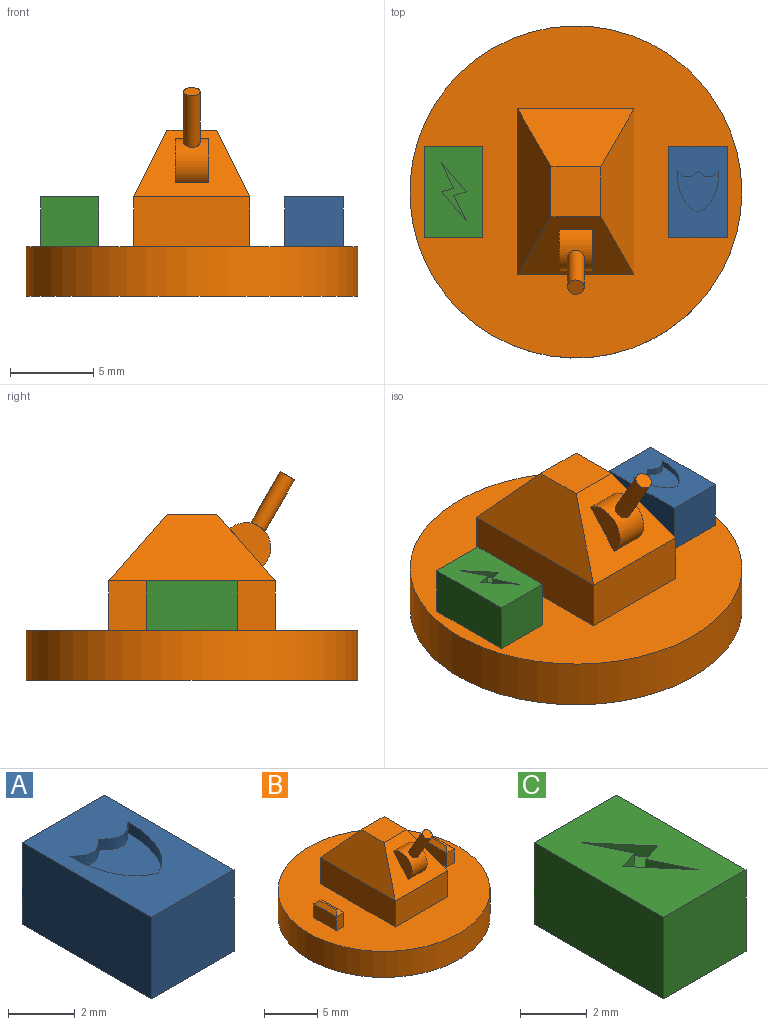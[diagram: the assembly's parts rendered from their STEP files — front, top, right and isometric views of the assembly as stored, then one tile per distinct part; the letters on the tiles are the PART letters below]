
ASSEMBLY  parts=3 mates=2
PART A: 16 faces, bbox 3.5x5.5x3 mm
  f0: plane 5.5x3.5mm, normal (0,0,1), area 15.1mm2, adj f4,f5,f6,f7,f11,f12,f13,f14
  f1: plane 2x1.5mm, normal (0,-1,0), area 3mm2, adj f2,f8,f9,f10
  f2: plane 3.5x2mm, normal (-1,0,0), area 7mm2, adj f1,f3,f9,f10
  f3: plane 2x1.5mm, normal (0,1,0), area 3mm2, adj f2,f8,f9,f10
  f4: plane 5.5x3mm, normal (1,0,0), area 16.5mm2, adj f0,f5,f7,f9
  f5: plane 3.5x3mm, normal (0,1,0), area 10.5mm2, adj f0,f4,f6,f9
  f6: plane 5.5x3mm, normal (-1,0,0), area 16.5mm2, adj f0,f5,f7,f9
  f7: plane 3.5x3mm, normal (0,-1,0), area 10.5mm2, adj f0,f4,f6,f9
  f8: plane 3.5x2mm, normal (1,0,0), area 7mm2, adj f1,f3,f9,f10
  f9: plane 5.5x3.5mm, normal (0,0,-1), area 14mm2, adj f1,f2,f3,f4,f5,f6,f7,f8
  f10: plane 3.5x1.5mm, normal (0,0,-1), area 5.2mm2, adj f1,f2,f3,f8
  f11: extruded ~1.25x0.4mm, area 0.6mm2, adj f0,f12,f14,f15
  f12: extruded ~1.25x0.4mm, area 0.6mm2, adj f0,f11,f13,f15
  f13: extruded ~2.5x1.25mm, area 1.2mm2, adj f0,f12,f14,f15
  f14: extruded ~2.5x1.25mm, area 1.2mm2, adj f0,f11,f13,f15
  f15: plane 2.5x2.5mm, normal (0,0,1), area 4.2mm2, adj f11,f12,f13,f14
PART B: 35 faces, bbox 20x20x12.6 mm
  f0: plane 20x20mm, normal (0,0,1), area 238.2mm2, adj f2,f3,f4,f5,f6,f22,f23,f24
  f1: plane 20x20mm, normal (0,0,-1), area 314.2mm2, adj f2
  f2: cylinder r=10mm len=20mm, axis (0,0,-1), area 188.5mm2, adj f0,f1
  f3: plane 7x3mm, normal (0,1,0), area 21mm2, adj f0,f4,f6,f9
  f4: plane 10x3mm, normal (-1,0,0), area 30mm2, adj f0,f3,f5,f10
  f5: plane 7x3mm, normal (0,-1,0), area 21mm2, adj f0,f4,f6,f11
  f6: plane 10x3mm, normal (1,0,0), area 30mm2, adj f0,f3,f5,f8
  f7: plane 3x3mm, normal (0,0,1), area 9mm2, adj f8,f9,f10,f11
  f8: plane 10x4mm, normal (0.89,0,0.45), area 29.1mm2, adj f6,f7,f9,f11
  f9: plane 7x4mm, normal (0,0.75,0.66), area 26.6mm2, adj f3,f7,f8,f10
  f10: plane 10x4mm, normal (-0.89,0,0.45), area 29.1mm2, adj f4,f7,f9,f11
  f11: plane 7x4mm, normal (0,-0.75,0.66), area 20.6mm2, adj f5,f7,f8,f10,f12,f13,f14
  f12: cylinder r=1.5mm len=2.63mm, axis (1,0,0), area 8.6mm2, adj f11,f13,f14,f16
  f13: plane 2.63x2.49mm, normal (-1,0,0), area 3.5mm2, adj f11,f12
  f14: plane 2.63x2.49mm, normal (1,0,0), area 3.5mm2, adj f11,f12
  f15: plane 1x0.87mm, normal (0,-0.5,0.87), area 0.8mm2, adj f16
  f16: cylinder r=0.5mm len=3.61mm, axis (0,0.5,-0.87), area 11.1mm2, adj f12,f15
  f17: plane 2.2x0.2mm, normal (0,0,1), area 0.4mm2, adj f18,f19,f20,f21
  f18: plane 3x0.4mm, normal (0.71,0,0.71), area 1.5mm2, adj f17,f19,f21,f25
  f19: plane 1x0.4mm, normal (0,0.71,0.71), area 0.3mm2, adj f17,f18,f20,f24
  f20: plane 3x0.4mm, normal (-0.71,0,0.71), area 1.5mm2, adj f17,f19,f21,f23
  f21: plane 1x0.4mm, normal (0,-0.71,0.71), area 0.3mm2, adj f17,f18,f20,f22
  f22: plane 1.6x1mm, normal (0,-1,0), area 1.6mm2, adj f0,f21,f23,f25
  f23: plane 3x1.6mm, normal (-1,0,0), area 4.8mm2, adj f0,f20,f22,f24
  f24: plane 1.6x1mm, normal (0,1,0), area 1.6mm2, adj f0,f19,f23,f25
  f25: plane 3x1.6mm, normal (1,0,0), area 4.8mm2, adj f0,f18,f22,f24
  f26: plane 2.2x0.2mm, normal (0,0,1), area 0.4mm2, adj f27,f28,f29,f30
  f27: plane 1x0.4mm, normal (0,0.71,0.71), area 0.3mm2, adj f26,f28,f30,f34
  f28: plane 3x0.4mm, normal (-0.71,0,0.71), area 1.5mm2, adj f26,f27,f29,f33
  f29: plane 1x0.4mm, normal (0,-0.71,0.71), area 0.3mm2, adj f26,f28,f30,f32
  f30: plane 3x0.4mm, normal (0.71,0,0.71), area 1.5mm2, adj f26,f27,f29,f31
  f31: plane 3x1.6mm, normal (1,0,0), area 4.8mm2, adj f0,f30,f32,f34
  f32: plane 1.6x1mm, normal (0,-1,0), area 1.6mm2, adj f0,f29,f31,f33
  f33: plane 3x1.6mm, normal (-1,0,0), area 4.8mm2, adj f0,f28,f32,f34
  f34: plane 1.6x1mm, normal (0,1,0), area 1.6mm2, adj f0,f27,f31,f33
PART C: 18 faces, bbox 3.5x5.5x3 mm
  f0: plane 5.5x3.5mm, normal (0,0,1), area 17.9mm2, adj f4,f5,f6,f7,f11,f12,f13,f14
  f1: plane 2x1.5mm, normal (0,-1,0), area 3mm2, adj f2,f8,f9,f10
  f2: plane 3.5x2mm, normal (-1,0,0), area 7mm2, adj f1,f3,f9,f10
  f3: plane 2x1.5mm, normal (0,1,0), area 3mm2, adj f2,f8,f9,f10
  f4: plane 5.5x3mm, normal (1,0,0), area 16.5mm2, adj f0,f5,f7,f9
  f5: plane 3.5x3mm, normal (0,1,0), area 10.5mm2, adj f0,f4,f6,f9
  f6: plane 5.5x3mm, normal (-1,0,0), area 16.5mm2, adj f0,f5,f7,f9
  f7: plane 3.5x3mm, normal (0,-1,0), area 10.5mm2, adj f0,f4,f6,f9
  f8: plane 3.5x2mm, normal (1,0,0), area 7mm2, adj f1,f3,f9,f10
  f9: plane 5.5x3.5mm, normal (0,0,-1), area 14mm2, adj f1,f2,f3,f4,f5,f6,f7,f8
  f10: plane 3.5x1.5mm, normal (0,0,-1), area 5.2mm2, adj f1,f2,f3,f8
  f11: plane 1.75x1.5mm, normal (-0.76,-0.65,0), area 0.9mm2, adj f0,f12,f16,f17
  f12: plane 1.53x0.75mm, normal (0.9,0.44,0), area 0.7mm2, adj f0,f11,f13,f17
  f13: plane 0.75x0.4mm, normal (0.28,-0.96,0), area 0.3mm2, adj f0,f12,f14,f17
  f14: plane 1.75x1.5mm, normal (0.76,0.65,0), area 0.9mm2, adj f0,f13,f15,f17
  f15: plane 1.53x0.75mm, normal (-0.9,-0.44,0), area 0.7mm2, adj f0,f14,f16,f17
  f16: plane 0.75x0.4mm, normal (-0.28,0.96,0), area 0.3mm2, adj f0,f11,f15,f17
  f17: plane 3.5x1.5mm, normal (0,0,1), area 1.3mm2, adj f11,f12,f13,f14,f15,f16
PLACE A t=(6.59,3.39,2.46)mm
PLACE B t=(-0.77,3.39,-0.54)mm fixed
PLACE C t=(-8.13,3.39,2.46)mm
MATE fastened C.f9 <-> B.f0  axis (0,0,-1) through (-8.13,3.39,2.46)mm
MATE fastened A.f9 <-> B.f0  axis (0,0,-1) through (6.59,3.39,2.46)mm
